# Revit family: 306_R2_P-_
name_source: partatom
category: Pipe Accessories
units: mm (PartAtom-declared; Revit-internal decimal feet)

## family parameters
Always vertical = Yes
Cut with Voids When Loaded = No
Part Type = Valve - Breaks Into
Round Connector Dimension = Use Diameter
Shared = No
Work Plane-Based = No

## types (13) — shared parameters
CAT0 = Yes
Description = Pressure independent characterised control valve, 2-way, Internal thread
L2D_Min = 3048 mm
M1 = 17 mm
MM = 21 mm  [stored 0.0688976 ft]
Manufacturer = Belimo
QmdConnectorList = 301;D;302;D
magiPartTypeId = 306
magiProductFamilyId = R2*P-*
zero-valued in all types: MC_Default_elevation

## per-type parameters (varying)
- R215P-010: C=63 mm; C__ve=-63 mm; CenSd_D4_6=8 mm  [stored 0.0262467 ft]; CenSd_DX1_6=11 mm; D=15 mm; D2=21 mm  [stored 0.0688976 ft]; D3=29 mm; D4=10 mm  [stored 0.0328084 ft]; DX1=13 mm; G=23 mm  [stored 0.0754593 ft]; H1=36 mm; H11=32 mm; H2=5 mm  [stored 0.0164042 ft]; H2__ve=-5 mm  [stored -0.0164042 ft]; H5=13 mm; L1=31 mm; L2=38 mm; L2D=114 mm; L3=47 mm; L4=22 mm  [stored 0.0721785 ft]; L5=14 mm  [stored 0.0459318 ft]; L5__ve=-14 mm; LL=57 mm; W2D=15 mm  [stored 0.0492126 ft]; XX1=21 mm  [stored 0.0688976 ft]; XX2=12 mm  [stored 0.0393701 ft]
- R250P-550: C=161 mm; C__ve=-161 mm; CenSd_D4_6=23 mm  [stored 0.0754593 ft]; CenSd_DX1_6=26 mm  [stored 0.0853018 ft]; D=50 mm; D2=56 mm; D3=64 mm; D4=27 mm  [stored 0.0885827 ft]; DX1=30 mm; G=58 mm; H1=76 mm; H11=67 mm; H2=10 mm  [stored 0.0328084 ft]; H2__ve=-10 mm  [stored -0.0328084 ft]; H5=34 mm; L1=126 mm; L2=83 mm; L2D=397 mm; L3=190 mm; L4=49 mm; L5=32 mm; L5__ve=-32 mm; LL=199 mm; W2D=50 mm; XX1=113 mm; XX2=65 mm
- R250P-270: C=93 mm; C__ve=-93 mm; CenSd_D4_6=23 mm  [stored 0.0754593 ft]; CenSd_DX1_6=26 mm  [stored 0.0853018 ft]; D=50 mm; D2=56 mm; D3=64 mm; D4=27 mm  [stored 0.0885827 ft]; DX1=30 mm; G=58 mm; H1=57 mm; H11=50 mm; H2=7 mm  [stored 0.0229659 ft]; H2__ve=-7 mm; H5=34 mm; L1=61 mm; L2=74 mm; L2D=225 mm; L3=92 mm; L4=43 mm; L5=29 mm; L5__ve=-29 mm; LL=113 mm; W2D=50 mm; XX1=40 mm; XX2=23 mm  [stored 0.0754593 ft]
- R240P-220: C=94 mm; C__ve=-94 mm; CenSd_D4_6=19 mm  [stored 0.062336 ft]; CenSd_DX1_6=22 mm  [stored 0.0721785 ft]; D=40 mm; D2=46 mm; D3=54 mm; D4=22 mm  [stored 0.0721785 ft]; DX1=25 mm  [stored 0.082021 ft]; G=48 mm; H1=51 mm; H11=45 mm; H2=6 mm  [stored 0.019685 ft]; H2__ve=-6 mm; H5=28 mm; L1=56 mm; L2=65 mm; L2D=204 mm; L3=85 mm; L4=38 mm; L5=25 mm  [stored 0.082021 ft]; L5__ve=-25 mm; LL=102 mm; W2D=40 mm; XX1=34 mm; XX2=19 mm  [stored 0.062336 ft]
- R240P-180: C=94 mm; C__ve=-94 mm; CenSd_D4_6=19 mm  [stored 0.062336 ft]; CenSd_DX1_6=22 mm  [stored 0.0721785 ft]; D=40 mm; D2=46 mm; D3=54 mm; D4=22 mm  [stored 0.0721785 ft]; DX1=25 mm  [stored 0.082021 ft]; G=48 mm; H1=51 mm; H11=45 mm; H2=6 mm  [stored 0.019685 ft]; H2__ve=-6 mm; H5=28 mm; L1=56 mm; L2=65 mm; L2D=204 mm; L3=85 mm; L4=38 mm; L5=25 mm  [stored 0.082021 ft]; L5__ve=-25 mm; LL=102 mm; W2D=40 mm; XX1=34 mm; XX2=19 mm  [stored 0.062336 ft]
- R232P-160: C=96 mm; C__ve=-96 mm; CenSd_D4_6=16 mm; CenSd_DX1_6=18 mm  [stored 0.0590551 ft]; D=32 mm; D2=38 mm; D3=46 mm; D4=18 mm  [stored 0.0590551 ft]; DX1=21 mm  [stored 0.0688976 ft]; G=40 mm; H1=51 mm; H11=45 mm; H2=6 mm  [stored 0.019685 ft]; H2__ve=-6 mm; H5=23 mm  [stored 0.0754593 ft]; L1=64 mm; L2=62 mm; L2D=221 mm; L3=97 mm; L4=36 mm; L5=24 mm  [stored 0.0787402 ft]; L5__ve=-24 mm  [stored -0.0787402 ft]; LL=111 mm; W2D=32 mm; XX1=43 mm; XX2=25 mm  [stored 0.082021 ft]
- R232P-120: C=96 mm; C__ve=-96 mm; CenSd_D4_6=16 mm; CenSd_DX1_6=18 mm  [stored 0.0590551 ft]; D=32 mm; D2=38 mm; D3=46 mm; D4=18 mm  [stored 0.0590551 ft]; DX1=21 mm  [stored 0.0688976 ft]; G=40 mm; H1=51 mm; H11=45 mm; H2=6 mm  [stored 0.019685 ft]; H2__ve=-6 mm; H5=23 mm  [stored 0.0754593 ft]; L1=64 mm; L2=62 mm; L2D=221 mm; L3=97 mm; L4=36 mm; L5=24 mm  [stored 0.0787402 ft]; L5__ve=-24 mm  [stored -0.0787402 ft]; LL=111 mm; W2D=32 mm; XX1=43 mm; XX2=25 mm  [stored 0.082021 ft]
- R225P-110: C=81 mm; C__ve=-81 mm; CenSd_D4_6=13 mm; CenSd_DX1_6=15 mm  [stored 0.0492126 ft]; D=25 mm; D2=31 mm; D3=39 mm; D4=15 mm  [stored 0.0492126 ft]; DX1=18 mm  [stored 0.0590551 ft]; G=33 mm; H1=46 mm; H11=40 mm; H2=6 mm  [stored 0.019685 ft]; H2__ve=-6 mm; H5=19 mm  [stored 0.062336 ft]; L1=47 mm; L2=63 mm; L2D=179 mm; L3=71 mm; L4=37 mm; L5=24 mm  [stored 0.0787402 ft]; L5__ve=-24 mm  [stored -0.0787402 ft]; LL=90 mm; W2D=25 mm  [stored 0.082021 ft]; XX1=34 mm; XX2=19 mm  [stored 0.062336 ft]
- R225P-070: C=81 mm; C__ve=-81 mm; CenSd_D4_6=13 mm; CenSd_DX1_6=15 mm  [stored 0.0492126 ft]; D=25 mm; D2=31 mm; D3=39 mm; D4=15 mm  [stored 0.0492126 ft]; DX1=18 mm  [stored 0.0590551 ft]; G=33 mm; H1=46 mm; H11=40 mm; H2=6 mm  [stored 0.019685 ft]; H2__ve=-6 mm; H5=19 mm  [stored 0.062336 ft]; L1=47 mm; L2=63 mm; L2D=179 mm; L3=71 mm; L4=37 mm; L5=24 mm  [stored 0.0787402 ft]; L5__ve=-24 mm  [stored -0.0787402 ft]; LL=90 mm; W2D=25 mm  [stored 0.082021 ft]; XX1=34 mm; XX2=19 mm  [stored 0.062336 ft]
- R220P-060: C=62 mm; C__ve=-62 mm; CenSd_D4_6=10 mm  [stored 0.0328084 ft]; CenSd_DX1_6=13 mm; D=20 mm; D2=26 mm  [stored 0.0853018 ft]; D3=34 mm; D4=12 mm  [stored 0.0393701 ft]; DX1=15 mm  [stored 0.0492126 ft]; G=28 mm; H1=36 mm; H11=32 mm; H2=5 mm  [stored 0.0164042 ft]; H2__ve=-5 mm  [stored -0.0164042 ft]; H5=16 mm; L1=34 mm; L2=43 mm; L2D=126 mm; L3=51 mm; L4=25 mm  [stored 0.082021 ft]; L5=16 mm; L5__ve=-16 mm; LL=63 mm; W2D=20 mm  [stored 0.0656168 ft]; XX1=20 mm  [stored 0.0656168 ft]; XX2=11 mm
- R220P-040: C=62 mm; C__ve=-62 mm; CenSd_D4_6=10 mm  [stored 0.0328084 ft]; CenSd_DX1_6=13 mm; D=20 mm; D2=26 mm  [stored 0.0853018 ft]; D3=34 mm; D4=12 mm  [stored 0.0393701 ft]; DX1=15 mm  [stored 0.0492126 ft]; G=28 mm; H1=36 mm; H11=32 mm; H2=5 mm  [stored 0.0164042 ft]; H2__ve=-5 mm  [stored -0.0164042 ft]; H5=16 mm; L1=34 mm; L2=43 mm; L2D=126 mm; L3=51 mm; L4=25 mm  [stored 0.082021 ft]; L5=16 mm; L5__ve=-16 mm; LL=63 mm; W2D=20 mm  [stored 0.0656168 ft]; XX1=20 mm  [stored 0.0656168 ft]; XX2=11 mm
- R215P-040: C=63 mm; C__ve=-63 mm; CenSd_D4_6=8 mm  [stored 0.0262467 ft]; CenSd_DX1_6=11 mm; D=15 mm; D2=21 mm  [stored 0.0688976 ft]; D3=29 mm; D4=10 mm  [stored 0.0328084 ft]; DX1=13 mm; G=23 mm  [stored 0.0754593 ft]; H1=36 mm; H11=32 mm; H2=5 mm  [stored 0.0164042 ft]; H2__ve=-5 mm  [stored -0.0164042 ft]; H5=13 mm; L1=31 mm; L2=38 mm; L2D=114 mm; L3=47 mm; L4=22 mm  [stored 0.0721785 ft]; L5=14 mm  [stored 0.0459318 ft]; L5__ve=-14 mm; LL=57 mm; W2D=15 mm  [stored 0.0492126 ft]; XX1=21 mm  [stored 0.0688976 ft]; XX2=12 mm  [stored 0.0393701 ft]
- R215P-020: C=63 mm; C__ve=-63 mm; CenSd_D4_6=8 mm  [stored 0.0262467 ft]; CenSd_DX1_6=11 mm; D=15 mm; D2=21 mm  [stored 0.0688976 ft]; D3=29 mm; D4=10 mm  [stored 0.0328084 ft]; DX1=13 mm; G=23 mm  [stored 0.0754593 ft]; H1=36 mm; H11=32 mm; H2=5 mm  [stored 0.0164042 ft]; H2__ve=-5 mm  [stored -0.0164042 ft]; H5=13 mm; L1=31 mm; L2=38 mm; L2D=114 mm; L3=47 mm; L4=22 mm  [stored 0.0721785 ft]; L5=14 mm  [stored 0.0459318 ft]; L5__ve=-14 mm; LL=57 mm; W2D=15 mm  [stored 0.0492126 ft]; XX1=21 mm  [stored 0.0688976 ft]; XX2=12 mm  [stored 0.0393701 ft]

note: column(s) folded — value = type name in every type: magiProductCode, magiProductId

note: [stored X ft] marks values corroborated as IEEE doubles in the binary element streams (Revit-internal decimal feet)

## geometry (parser evidence)
native form markers: Sweep x1
no freeform markers — native parametric forms only
